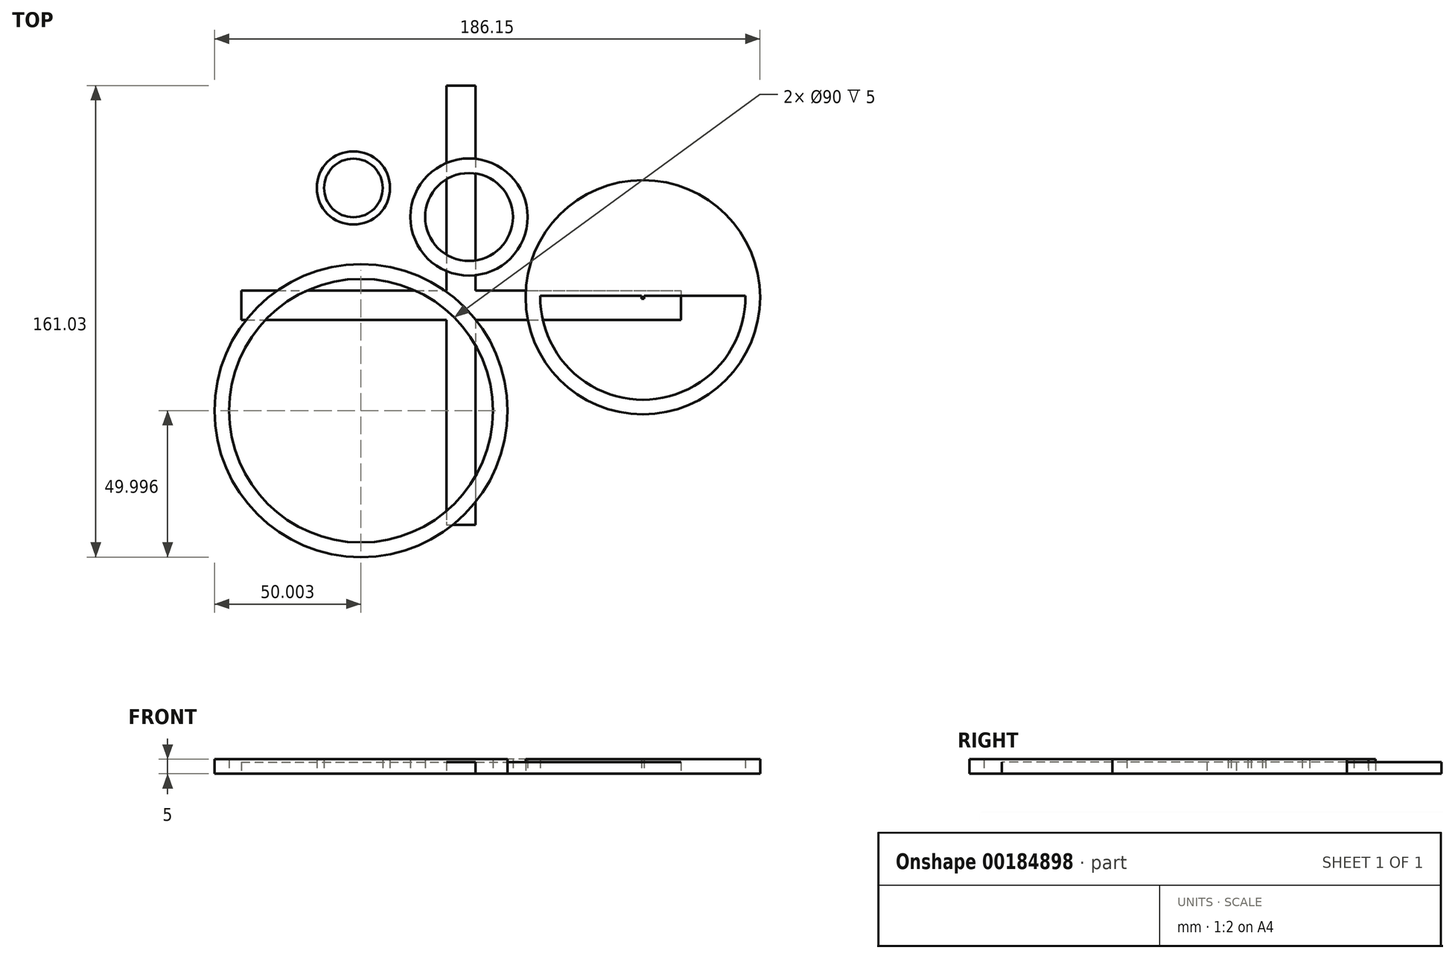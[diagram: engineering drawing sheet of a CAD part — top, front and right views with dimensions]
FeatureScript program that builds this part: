
annotation { "Feature Type Name" : "Feature", "Feature Type Description" : "" }
export const myFeature = defineFeature(function(context is Context, id is Id, definition is map)
    precondition{}
    {
        {
            var Q0;
            Q0=qCreatedBy(makeId("Top.planeOp"),FACE);
            var sketch = newSketch(context, id + "F0", { "sketchPlane" : qUnion([Q0])});
            skLineSegment(sketch, "E0.bottom", {"start": v(-5, 75) * mm, "end": v(5, 75) * mm});
            skLineSegment(sketch, "E0.top", {"start": v(-5, -75) * mm, "end": v(5, -75) * mm});
            skLineSegment(sketch, "E0.left", {"start": v(-5, 75) * mm, "end": v(-5, -75) * mm});
            skLineSegment(sketch, "E0.right", {"start": v(5, 75) * mm, "end": v(5, -75) * mm});
            skPoint(sketch, "E1", {"position": v(-5, 0) * mm});
            skPoint(sketch, "E2", {"position": v(0, 75) * mm});
            skLineSegment(sketch, "E3.bottom", {"start": v(-75, 5) * mm, "end": v(75, 5) * mm});
            skLineSegment(sketch, "E3.top", {"start": v(-75, -5) * mm, "end": v(75, -5) * mm});
            skLineSegment(sketch, "E3.left", {"start": v(-75, 5) * mm, "end": v(-75, -5) * mm});
            skLineSegment(sketch, "E3.right", {"start": v(75, 5) * mm, "end": v(75, -5) * mm});
            skPoint(sketch, "E4", {"position": v(0, 5) * mm});
            skPoint(sketch, "E5", {"position": v(-75, 0) * mm});
            skSolve(sketch);
        }
        {
            var Q0;
            Q0 = qSketchRegion(id + "F0", true);
            extrude(context, id + "F1", {"entities" : qUnion([Q0]), "depth" : 4 * mm});
        }
        {
            var Q0;
            Q0=qCreatedBy(makeId("Top.planeOp"),FACE);
            var sketch = newSketch(context, id + "F2", { "sketchPlane" : qUnion([Q0])});
            skCircle(sketch, "E6", {"center": v(-36.72, 40.03) * mm, "radius": 10 * mm});
            skCircle(sketch, "E7", {"center": v(-36.72, 40.03) * mm, "radius": 12.5 * mm});
            skCircle(sketch, "E8", {"center": v(2.74, 30.11) * mm, "radius": 15 * mm});
            skCircle(sketch, "E9", {"center": v(2.74, 30.11) * mm, "radius": 20 * mm});
            skCircle(sketch, "E10", {"center": v(62.03, 2.7) * mm, "radius": 35 * mm});
            skCircle(sketch, "E11", {"center": v(62.03, 2.7) * mm, "radius": 40 * mm});
            skCircle(sketch, "E12", {"center": v(-34.12, -36.03) * mm, "radius": 45 * mm});
            skCircle(sketch, "E13", {"center": v(-34.12, -36.03) * mm, "radius": 50 * mm});
            skLineSegment(sketch, "E14", {"start": v(22.03, 2.7) * mm, "end": v(102.03, 2.7) * mm, "construction": true});
            skLineSegment(sketch, "E15", {"start": v(62.03, -37.3) * mm, "end": v(62.03, 42.7) * mm, "construction": true});
            skLineSegment(sketch, "E16.0", {"start": v(22.03, 2.2) * mm, "end": v(102.03, 2.2) * mm});
            skLineSegment(sketch, "E17.0", {"start": v(22.03, 3.2) * mm, "end": v(102.03, 3.2) * mm});
            skLineSegment(sketch, "E18.0", {"start": v(62.53, -37.3) * mm, "end": v(62.53, 42.7) * mm});
            skLineSegment(sketch, "E19.0", {"start": v(61.53, -37.3) * mm, "end": v(61.53, 42.7) * mm});
            skSolve(sketch);
        }
        {
            var Q0;
            Q0 = qSketchRegion(id + "F2", true);
            var Q1;
            {var subQ0=sQuery(id+"F2.wireOp",EDGE,"E18.0");var subQ1=sQuery(id+"F2.wireOp",EDGE,"E10");var subQ2=makeQuery(id+"F2.imprint","INTERSECT",VERTEX,{"disambiguationData":[OD(0.0)],"derivedFrom":[subQ1,subQ0]});Q1=makeQuery(id+"F2.imprint","IMPRINT",FACE,{"disambiguationData":[TD([[makeQuery(id+"F2.imprint","IMPRINT",EDGE,{"disambiguationData":[TD([[subQ2,-1.0]])],"derivedFrom":subQ1}),1.0]])]});}
            var Q2;
            {var subQ0=sQuery(id+"F2.wireOp",EDGE,"E17.0");var subQ1=sQuery(id+"F2.wireOp",EDGE,"E10");var subQ2=makeQuery(id+"F2.imprint","INTERSECT",VERTEX,{"disambiguationData":[OD(1.0)],"derivedFrom":[subQ1,subQ0]});Q2=makeQuery(id+"F2.imprint","IMPRINT",FACE,{"disambiguationData":[TD([[makeQuery(id+"F2.imprint","IMPRINT",EDGE,{"disambiguationData":[TD([[subQ2,-1.0]])],"derivedFrom":subQ1}),1.0]])]});}
            var Q3;
            {var subQ0=sQuery(id+"F2.wireOp",EDGE,"E17.0");var subQ1=sQuery(id+"F2.wireOp",EDGE,"E10");var subQ2=makeQuery(id+"F2.imprint","INTERSECT",VERTEX,{"disambiguationData":[OD(0.0)],"derivedFrom":[subQ1,subQ0]});Q3=makeQuery(id+"F2.imprint","IMPRINT",FACE,{"disambiguationData":[TD([[makeQuery(id+"F2.imprint","IMPRINT",EDGE,{"disambiguationData":[TD([[subQ2,1.0]])],"derivedFrom":subQ1}),1.0]])]});}
            var Q4;
            {var subQ0=sQuery(id+"F2.wireOp",EDGE,"E19.0");var subQ1=sQuery(id+"F2.wireOp",EDGE,"E16.0");var subQ2=makeQuery(id+"F2.imprint","INTERSECT",VERTEX,{"derivedFrom":[subQ1,subQ0]});Q4=makeQuery(id+"F2.imprint","IMPRINT",FACE,{"disambiguationData":[TD([[makeQuery(id+"F2.imprint","IMPRINT",EDGE,{"disambiguationData":[TD([[subQ2,-1.0]])],"derivedFrom":subQ1}),1.0]])]});}
            var Q5;
            {var subQ0=sQuery(id+"F2.wireOp",EDGE,"E19.0");var subQ1=sQuery(id+"F2.wireOp",EDGE,"E10");var subQ2=makeQuery(id+"F2.imprint","INTERSECT",VERTEX,{"disambiguationData":[OD(1.0)],"derivedFrom":[subQ1,subQ0]});Q5=makeQuery(id+"F2.imprint","IMPRINT",FACE,{"disambiguationData":[TD([[makeQuery(id+"F2.imprint","IMPRINT",EDGE,{"disambiguationData":[TD([[subQ2,-1.0]])],"derivedFrom":subQ1}),1.0]])]});}
            extrude(context, id + "F3", {"entities" : qUnion([Q0, Q1, Q2, Q3, Q4, Q5]), "depth" : 5 * mm});
        }
    });
